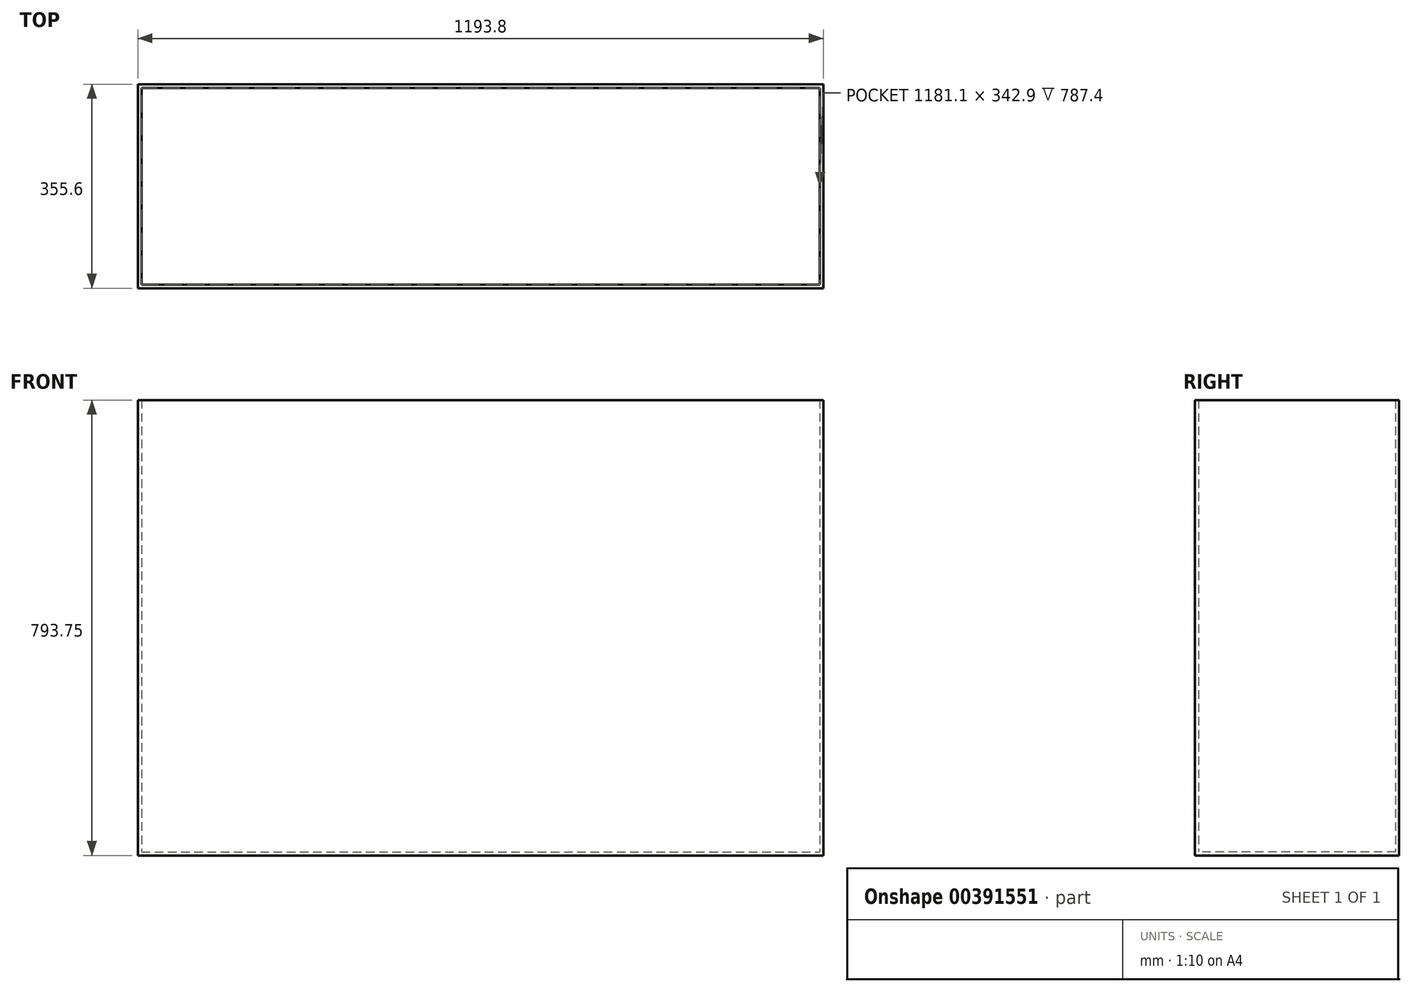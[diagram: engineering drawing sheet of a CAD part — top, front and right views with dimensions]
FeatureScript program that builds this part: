
annotation { "Feature Type Name" : "Feature", "Feature Type Description" : "" }
export const myFeature = defineFeature(function(context is Context, id is Id, definition is map)
    precondition{}
    {
        {
            var Q0;
            Q0=qCreatedBy(makeId("Top.planeOp"),FACE);
            var sketch = newSketch(context, id + "F0", { "sketchPlane" : qUnion([Q0])});
            skLineSegment(sketch, "E0.bottom", {"start": v(0, 0) * mm, "end": v(1193.8, 0) * mm});
            skLineSegment(sketch, "E0.top", {"start": v(0, -355.6) * mm, "end": v(1193.8, -355.6) * mm});
            skLineSegment(sketch, "E0.left", {"start": v(0, 0) * mm, "end": v(0, -355.6) * mm});
            skLineSegment(sketch, "E0.right", {"start": v(1193.8, 0) * mm, "end": v(1193.8, -355.6) * mm});
            skLineSegment(sketch, "E1.0", {"start": v(6.35, -6.35) * mm, "end": v(1187.45, -6.35) * mm});
            skLineSegment(sketch, "E1.1", {"start": v(6.35, -6.35) * mm, "end": v(6.35, -349.25) * mm});
            skLineSegment(sketch, "E1.2", {"start": v(6.35, -349.25) * mm, "end": v(1187.45, -349.25) * mm});
            skLineSegment(sketch, "E1.3", {"start": v(1187.45, -6.35) * mm, "end": v(1187.45, -349.25) * mm});
            skSolve(sketch);
        }
        {
            var Q0;
            Q0=makeQuery(id+"F0.imprint","IMPRINT",FACE,{"disambiguationData":[TD([[makeQuery(id+"F0.imprint","IMPRINT",EDGE,{"derivedFrom":sQuery(id+"F0.wireOp",EDGE,"E0.bottom")}),-1.0]])]});
            extrude(context, id + "F1", {"entities" : qUnion([Q0]), "depth" : 787.4 * mm});
        }
        {
            var Q0;
            Q0=makeQuery(id+"F1.opExtrude","CAP_FACE",FACE,{"disambiguationData":[OSD([sQuery(id+"F0.wireOp",EDGE,"E0.bottom"),sQuery(id+"F0.wireOp",EDGE,"E0.top"),sQuery(id+"F0.wireOp",EDGE,"E0.left"),sQuery(id+"F0.wireOp",EDGE,"E0.right"),sQuery(id+"F0.wireOp",EDGE,"E1.0"),sQuery(id+"F0.wireOp",EDGE,"E1.1"),sQuery(id+"F0.wireOp",EDGE,"E1.2"),sQuery(id+"F0.wireOp",EDGE,"E1.3")])],"isStart":true});
            var sketch = newSketch(context, id + "F2", { "sketchPlane" : qUnion([Q0])});
            skLineSegment(sketch, "E2.0", {"start": v(0, 0) * mm, "end": v(0, 355.6) * mm});
            skLineSegment(sketch, "E2.1", {"start": v(0, 355.6) * mm, "end": v(1193.8, 355.6) * mm});
            skLineSegment(sketch, "E2.2", {"start": v(1193.8, 0) * mm, "end": v(1193.8, 355.6) * mm});
            skLineSegment(sketch, "E2.3", {"start": v(0, 0) * mm, "end": v(1193.8, 0) * mm});
            skSolve(sketch);
        }
        {
            var Q0;
            Q0 = qSketchRegion(id + "F2", true);
            extrude(context, id + "F3", {"entities" : qUnion([Q0]), "operationType" : NewBodyOperationType.ADD, "depth" : 6.35 * mm});
        }
    });
